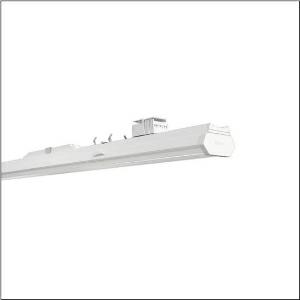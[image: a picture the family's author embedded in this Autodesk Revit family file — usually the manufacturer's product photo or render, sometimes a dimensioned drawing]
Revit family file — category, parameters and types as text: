
# Revit family: licross_r__11_protected_mo_51tp12dn595gd_f591
name_source: partatom
category: Lighting Fixtures
units: mm (PartAtom-declared; Revit-internal decimal feet)

## family parameters
Cut with Voids When Loaded = No
Host = Face
Light Source = No
Part Type = Normal
Room Calculation Point = No
Round Connector Dimension = Use Diameter
Shared = No

## types (1)
- --- (1 x LED, 1580 lm, 9.9 W, 5000K)
    Apparent Load = 10 VA
    CIE Flux Codes = 73 92 98 99 100
    Color Rendering = 80
    Color Temperature = 5000K
    Default Elevation = 1800 mm
    Description = Licross® 11 Protected MO, luminaire insert, of sheet steel, galvanised, coil coated, white, length: 1.500mm, width: 90mm, height: 101mm, LED rated luminous flux: 9.820lm, light colour: 850, control gear: DALI 2 (for two DALI lines), with plug, 6-pole, with phase selection, mains connection: 220..240V, AC/DC, 0/50..60Hz, rated input power: 57W, internal wiring halogen-free, for central battery installations according to DIN EN 60598-2-22, for emergency light function, without changeover relay, primary optical cover: cover, of PMMA, light emission: direct distribution, primary light characteristic: symmetric, protection rating (complete): IP64, insulation class (complete): insulation class I (protective earthing), certification: CE, ENEC, VDE, UKCA, protection symbol: D if used in an environment without relevant dust loads with corresponding accessories, impact resistance: IK06, permissible ambient temperature for indoor applications: -25..+35°C, standard: EN 60598-2-22, corresponds to IFS (International Featured Standards) requirements for safety and quality in the food industry, reducing of maximum allowable ambient temperature of 5°C with ceiling mounting, LABS conformity tested according to VDMA 24364:2018-05, packaging unit: 1 piece
    Height = 92 mm
    Lamp = 1 x LED
    Lamp Light Flux = 1580 lm
    Lamp Power = 9.9 W
    Lamp count = 1
    Length = 1500 mm
    Luminous efficacy = 160 lm/W
    Manufacturer = Siteco
    ModVariant = No
    Model = 51TP12DN595GD
    Mounting Place = Ceiling
    Mounting Type = Pendant
    Number of Poles = 1
    OnlyDefault = Yes
    Power Factor = 1
    Product Name = Licross® 11 Protected MO
    Product group = luminaire insert | ceiling pendant
    ProductGroupID = 902
    Protection Class = Protection class I
    Protection Degree = IP 64
    RLX_Detail_Level = 1
    RLX_Emergency_Light_Flux = 0 lm
    RLX_Emergency_Type = 0
    RLX_Emergency_Type_DB = No
    RlxData = <blob elided: 24885 chars, md5=40b57df9>
    Socket = socket
    Standby Power = 0 W
    System Light Flux = 1580 lm
    System Power = 10 W
    Type Comments = : DC mode (central or group accumulator) initial emergency light level
    Type Image = l_1256148.jpg
    URL = http://relux.com
    VarID = @adj_042615
    Voltage = 0 V
    Weight = 0.00 kg
    Width = 88 mm

## geometry (parser evidence)
native form markers: Blend x4, Sweep x10
no freeform markers — native parametric forms only
